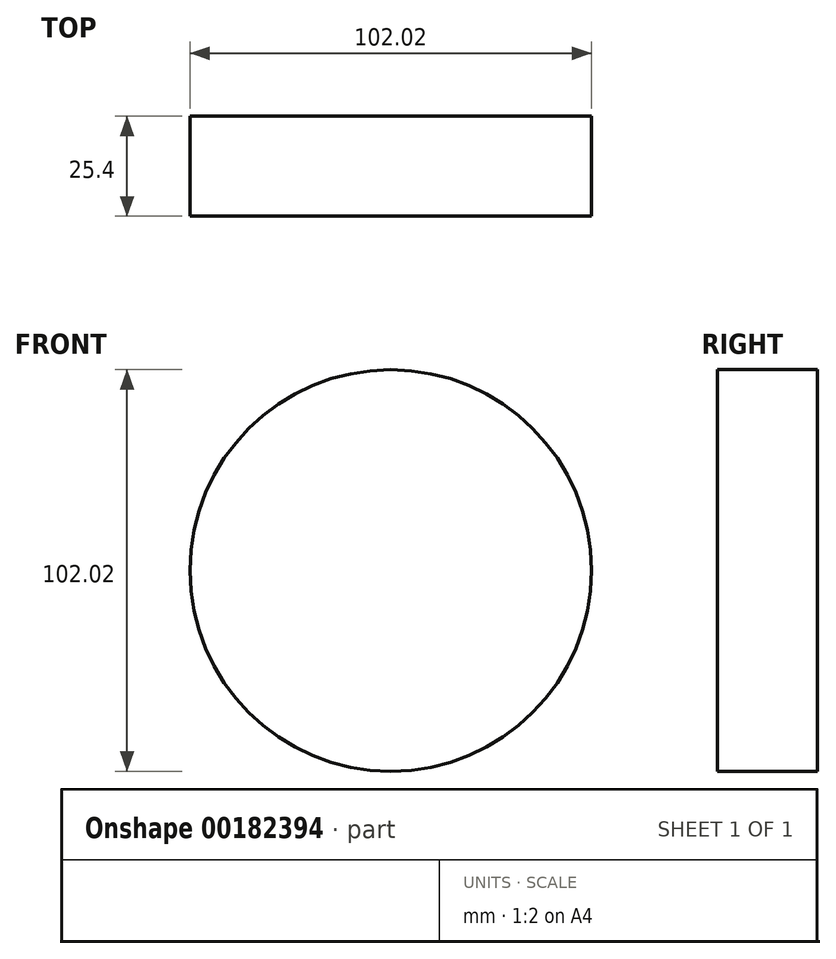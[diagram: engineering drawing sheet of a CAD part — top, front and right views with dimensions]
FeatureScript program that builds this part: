
annotation { "Feature Type Name" : "Feature", "Feature Type Description" : "" }
export const myFeature = defineFeature(function(context is Context, id is Id, definition is map)
    precondition{}
    {
        {
            var Q0;
            Q0=qCreatedBy(makeId("Front.planeOp"),FACE);
            var sketch = newSketch(context, id + "F0", { "sketchPlane" : qUnion([Q0])});
            skCircle(sketch, "E0", {"center": v(0, 0) * mm, "radius": 51 * mm});
            skSolve(sketch);
        }
        {
            var Q0;
            Q0=makeQuery(id+"F0.imprint","IMPRINT",FACE,{"disambiguationData":[TD([[makeQuery(id+"F0.imprint","IMPRINT",EDGE,{"derivedFrom":sQuery(id+"F0.wireOp",EDGE,"E0")}),1.0]])]});
            extrude(context, id + "F1", {"entities" : qUnion([Q0]), "depth" : 25.4 * mm});
        }
    });
